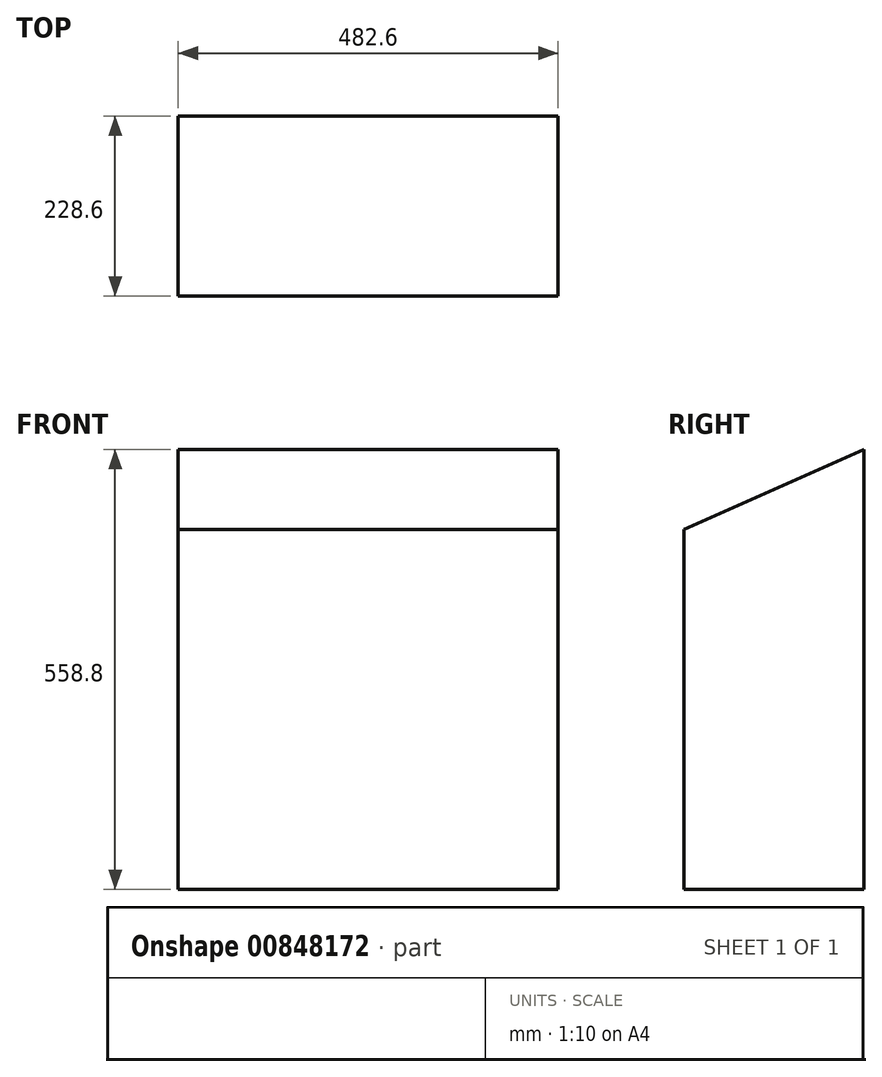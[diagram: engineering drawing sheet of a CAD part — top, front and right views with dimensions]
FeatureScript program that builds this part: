
annotation { "Feature Type Name" : "Feature", "Feature Type Description" : "" }
export const myFeature = defineFeature(function(context is Context, id is Id, definition is map)
    precondition{}
    {
        {
            var Q0;
            Q0=qCreatedBy(makeId("Right.planeOp"),FACE);
            var sketch = newSketch(context, id + "F0", { "sketchPlane" : qUnion([Q0])});
            skLineSegment(sketch, "E0.bottom", {"start": v(0, 0) * mm, "end": v(228.6, 0) * mm});
            skLineSegment(sketch, "E0.top", {"start": v(0, 558.8) * mm, "end": v(228.6, 558.8) * mm});
            skLineSegment(sketch, "E0.left", {"start": v(0, 0) * mm, "end": v(0, 558.8) * mm});
            skLineSegment(sketch, "E0.right", {"start": v(228.6, 0) * mm, "end": v(228.6, 558.8) * mm});
            skSolve(sketch);
        }
        {
            var Q0;
            Q0=makeQuery(id+"F0.imprint","IMPRINT",FACE,{"disambiguationData":[TD([[makeQuery(id+"F0.imprint","IMPRINT",EDGE,{"derivedFrom":sQuery(id+"F0.wireOp",EDGE,"E0.bottom")}),1.0]])]});
            extrude(context, id + "F1", {"entities" : qUnion([Q0]), "oppositeDirection" : true, "depth" : 482.6 * mm, "offsetDistance" : 25.4 * mm});
        }
        {
            var Q0;
            Q0=makeQuery(id+"F1.opExtrude","SWEPT_EDGE",EDGE,{"disambiguationData":[OSD([sQuery(id+"F0.wireOp",EDGE,"E0.top"),sQuery(id+"F0.wireOp",EDGE,"E0.left")])]});
            chamfer(context, id + "F2", {"entities" : qUnion([Q0]), "chamferType" : ChamferType.TWO_OFFSETS, "width1" : 228.6 * mm, "oppositeDirection" : false, "width2" : 101.6 * mm, "tangentPropagation" : true});
        }
    });
